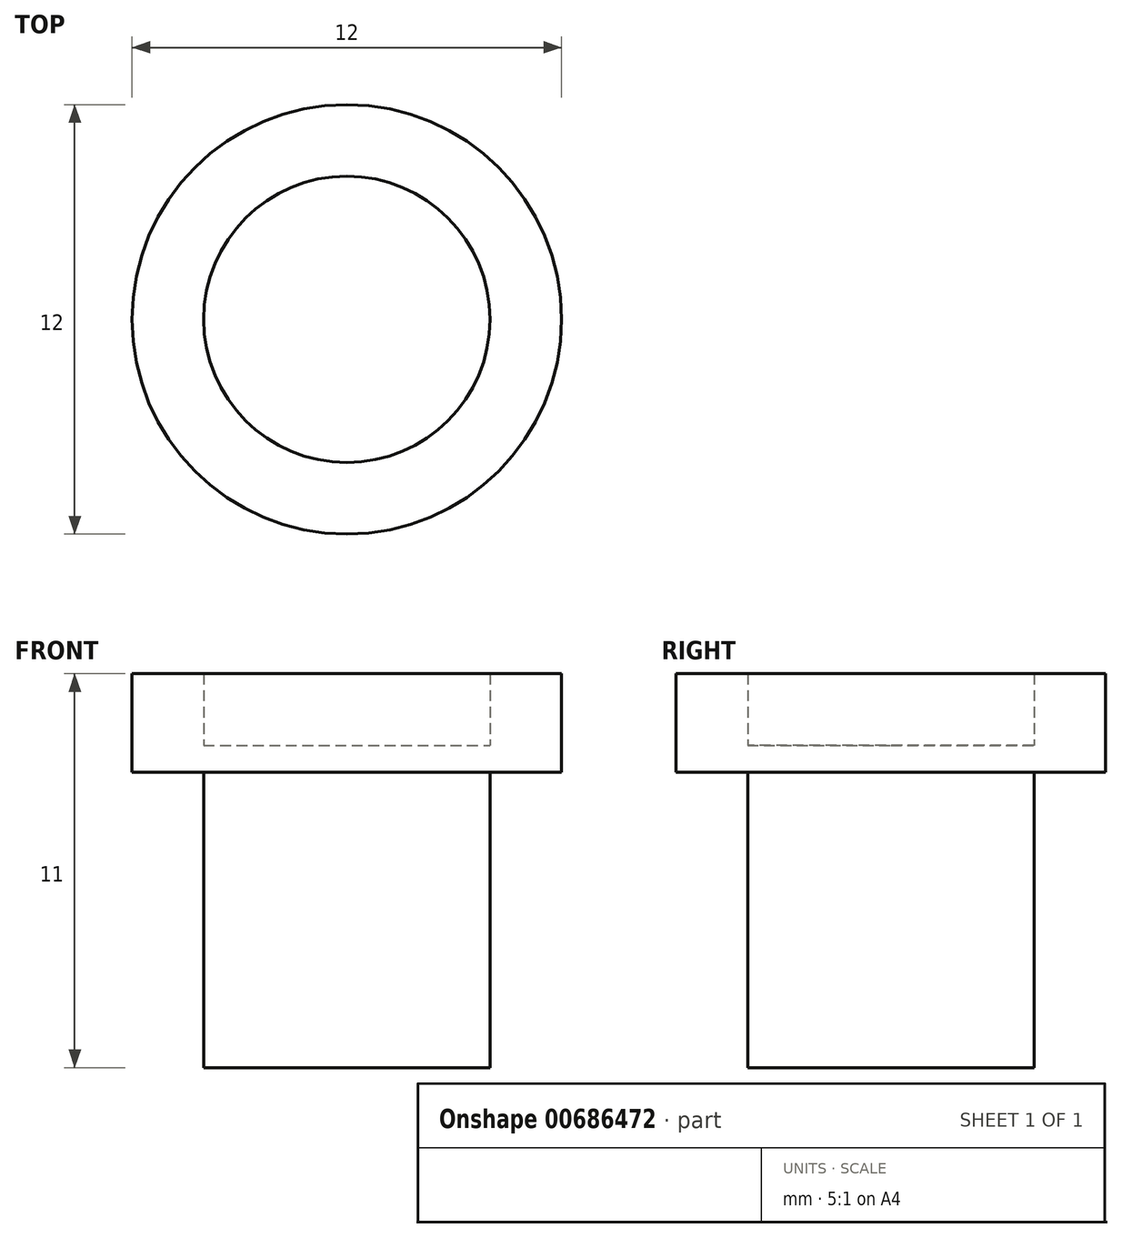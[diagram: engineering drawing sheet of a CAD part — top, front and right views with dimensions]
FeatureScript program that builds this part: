
annotation { "Feature Type Name" : "Feature", "Feature Type Description" : "" }
export const myFeature = defineFeature(function(context is Context, id is Id, definition is map)
    precondition{}
    {
        {
            var Q0;
            Q0=qCreatedBy(makeId("Front.planeOp"),FACE);
            var sketch = newSketch(context, id + "F0", { "sketchPlane" : qUnion([Q0])});
            skLineSegment(sketch, "E0.bottom", {"start": v(0, 0) * mm, "end": v(4, 0) * mm});
            skLineSegment(sketch, "E0.left", {"start": v(0, 0) * mm, "end": v(0, 8) * mm});
            skLineSegment(sketch, "E0.right", {"start": v(4, 0) * mm, "end": v(4, 8.25) * mm});
            skLineSegment(sketch, "E1.top", {"start": v(0, 9) * mm, "end": v(4, 9) * mm});
            skLineSegment(sketch, "E1.left", {"start": v(0, 8) * mm, "end": v(0, 9) * mm});
            skPoint(sketch, "E1.bottom.end.orphan", {"position": v(8, 8) * mm});
            skLineSegment(sketch, "E2.bottom", {"start": v(4, 8.25) * mm, "end": v(6, 8.25) * mm});
            skLineSegment(sketch, "E2.top", {"start": v(4, 11) * mm, "end": v(6, 11) * mm});
            skLineSegment(sketch, "E2.left", {"start": v(4, 8.25) * mm, "end": v(4, 11) * mm});
            skLineSegment(sketch, "E2.right", {"start": v(6, 8.25) * mm, "end": v(6, 11) * mm});
            skSolve(sketch);
        }
        {
            var Q0;
            Q0=makeQuery(id+"F0.imprint","IMPRINT",FACE,{"disambiguationData":[TD([[makeQuery(id+"F0.imprint","IMPRINT",EDGE,{"derivedFrom":sQuery(id+"F0.wireOp",EDGE,"E0.bottom")}),1.0]])]});
            var Q1;
            {var subQ3=sQuery(id+"F0.wireOp",EDGE,"E2.bottom");Q1=makeQuery(id+"F0.imprint","IMPRINT",FACE,{"disambiguationData":[TD([[makeQuery(id+"F0.imprint","IMPRINT",EDGE,{"derivedFrom":subQ3}),1.0]])]});}
            var Q2;
            Q2=sQuery(id+"F0.wireOp",EDGE,"E0.left");
            revolve(context, id + "F1", {"entities" : qUnion([Q0, Q1]), "axis" : qUnion([Q2]), "revolveType" : RevolveType.FULL});
        }
    });
